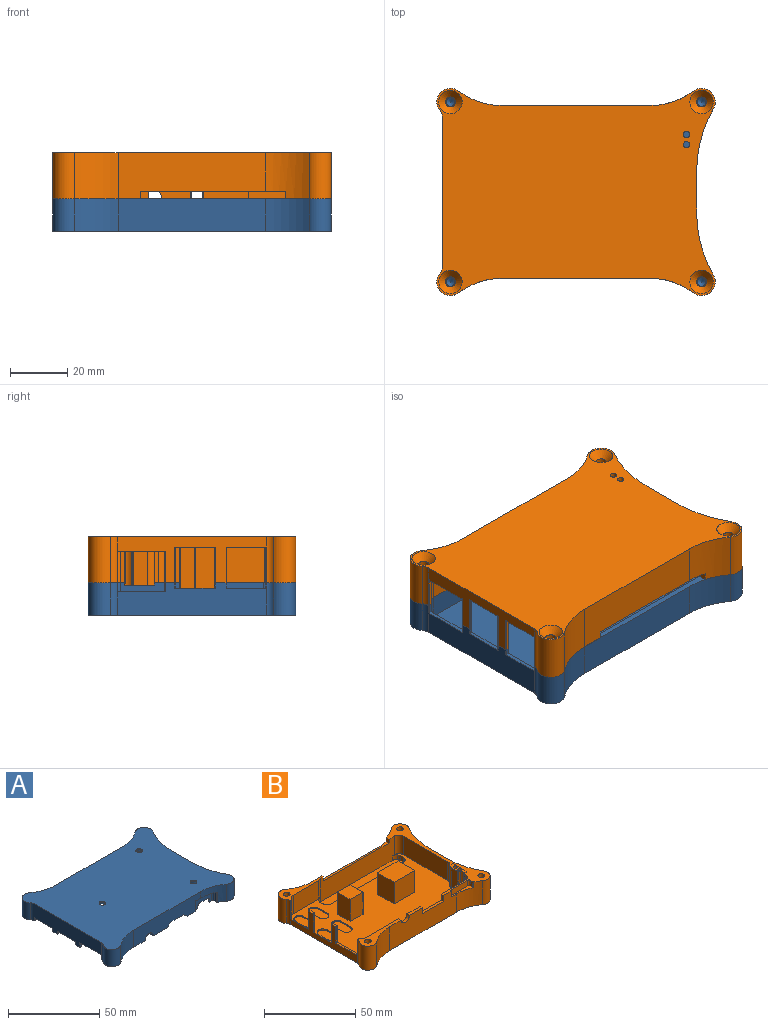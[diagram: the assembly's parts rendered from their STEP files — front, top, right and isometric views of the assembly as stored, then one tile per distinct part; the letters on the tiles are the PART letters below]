
ASSEMBLY  parts=2 mates=1
PART A: 96 faces, bbox 97.3x72.4x11.4 mm
  f0: cylinder r=1.6mm len=1.6mm, axis (0,-1,0), area 2.4mm2, adj f1,f2,f45,f55
  f1: plane 1.58x0.96mm, normal (1,0,0), area 1.5mm2, adj f0,f45,f55,f72
  f2: plane 5.69x0.96mm, normal (0,0,-1), area 5.5mm2, adj f0,f45,f47,f55
  f3: plane 11.74x2.84mm, normal (1,0,0), area 33.4mm2, adj f6,f8,f11,f71
  f4: plane 11.49x2.84mm, normal (0,-1,0), area 32.7mm2, adj f5,f6,f8,f71
  f5: cylinder r=0.25mm len=2.85mm, axis (0,0,1), area 1.1mm2, adj f4,f6,f7,f71
  f6: plane 12.25x12mm, normal (0,0,-1), area 146.9mm2, adj f3,f4,f5,f7,f8,f9,f10,f11
  f7: plane 11.74x2.84mm, normal (-1,0,0), area 33.4mm2, adj f5,f6,f9,f71
  f8: cylinder r=0.25mm len=2.85mm, axis (0,0,1), area 1.1mm2, adj f3,f4,f6,f71
  f9: cylinder r=0.25mm len=2.85mm, axis (0,0,1), area 1.1mm2, adj f6,f7,f10,f71
  f10: plane 11.49x2.84mm, normal (0,1,0), area 32.7mm2, adj f6,f9,f11,f71
  f11: cylinder r=0.25mm len=2.85mm, axis (0,0,1), area 1.1mm2, adj f3,f6,f10,f71
  f12: cylinder r=0.25mm len=2.03mm, axis (0,0,1), area 0.8mm2, adj f19,f57,f94,f95
  f13: cylinder r=0.23mm len=2.03mm, axis (0,0,-1), area 0.6mm2, adj f19,f43,f69,f70
  f14: cylinder r=3.43mm len=11.43mm, axis (0,0,-1), area 27.9mm2, adj f20,f25,f38,f70,f92
  f15: plane 16.88x1.44mm, normal (0,0,-1), area 19.7mm2, adj f16,f17,f18,f37,f44,f57,f66,f67
  f16: cylinder r=0.25mm len=3.23mm, axis (0,0,1), area 1.3mm2, adj f15,f17,f57,f65
  f17: plane 3.23x0.69mm, normal (0,-1,0), area 2.2mm2, adj f15,f16,f18,f65
  f18: cylinder r=0.25mm len=3.23mm, axis (0,0,1), area 1.3mm2, adj f15,f17,f65,f92
  f19: plane 14.2x1.4mm, normal (0,0,-1), area 16.5mm2, adj f12,f13,f20,f43,f57,f69,f92,f93
  f20: cylinder r=0.23mm len=2.03mm, axis (0,0,-1), area 0.7mm2, adj f14,f19,f69,f70
  f21: cylinder r=1.83mm len=3.66mm, axis (0,0,1), area 9mm2, adj f24,f38
  f22: cylinder r=1.83mm len=3.66mm, axis (0,0,1), area 9mm2, adj f23,f38
  f23: cone r=1.83mm half-angle=41deg, axis (0,0,-1), area 63.9mm2, adj f22,f71
  f24: cone r=1.77mm half-angle=41deg, axis (0,0,-1), area 63.9mm2, adj f21,f71
  f25: cylinder r=4.76mm len=11.43mm, axis (0,0,-1), area 159.2mm2, adj f14,f26,f38,f70
  f26: cylinder r=25.4mm len=15.24mm, axis (0,0,-1), area 186.8mm2, adj f25,f27,f38,f70
  f27: plane 51.56x11.43mm, normal (0,1,0), area 589.4mm2, adj f26,f28,f38,f70
  f28: cylinder r=25.4mm len=15.24mm, axis (0,0,-1), area 186.8mm2, adj f27,f29,f38,f70
  f29: cylinder r=4.76mm len=11.43mm, axis (0,0,-1), area 148.8mm2, adj f28,f30,f38,f70
  f30: cylinder r=44.45mm len=22.05mm, axis (0,0,-1), area 263.7mm2, adj f29,f31,f38,f70
  f31: plane 14.04x11.43mm, normal (1,0,0), area 140.5mm2, adj f30,f32,f38,f70,f80,f81,f82,f83
  f32: cylinder r=44.45mm len=22.05mm, axis (0,0,-1), area 263.7mm2, adj f31,f33,f38,f70
  f33: cylinder r=4.76mm len=11.43mm, axis (0,0,-1), area 148.8mm2, adj f32,f34,f38,f70
  f34: cylinder r=25.4mm len=15.24mm, axis (0,0,-1), area 108.6mm2, adj f33,f38,f46,f51,f52,f70
  f35: cylinder r=25.4mm len=15.24mm, axis (0,0,-1), area 186.8mm2, adj f36,f38,f46,f49
  f36: cylinder r=4.76mm len=11.43mm, axis (0,0,-1), area 159.2mm2, adj f35,f37,f38,f49
  f37: cylinder r=3.43mm len=11.43mm, axis (0,0,-1), area 27.5mm2, adj f15,f36,f38,f49,f66,f92
  f38: plane 97.28x72.39mm, normal (0,0,1), area 5689.1mm2, adj f14,f21,f22,f25,f26,f27,f28,f29
  f39: cylinder r=3.43mm len=8.05mm, axis (0,0,1), area 43.4mm2, adj f40,f45,f70,f71
  f40: plane 49.66x8.05mm, normal (-1,0,0), area 379.9mm2, adj f39,f41,f70,f71,f80,f81,f82,f83
  f41: cylinder r=3.43mm len=8.05mm, axis (0,0,1), area 43.4mm2, adj f40,f42,f70,f71
  f42: plane 78.74x8.05mm, normal (0,-1,0), area 634mm2, adj f41,f43,f70,f71
  f43: cylinder r=3.43mm len=8.05mm, axis (0,0,1), area 40.9mm2, adj f13,f19,f42,f57,f70,f71
  f44: cylinder r=3.43mm len=8.05mm, axis (0,0,1), area 39.2mm2, adj f15,f45,f49,f57,f68,f71
  f45: plane 78.74x8.05mm, normal (0,1,0), area 558.8mm2, adj f0,f1,f2,f39,f44,f47,f48,f49
  f46: plane 51.56x11.43mm, normal (0,-1,0), area 513.2mm2, adj f34,f35,f38,f49,f50,f51,f72,f73
  f47: cylinder r=1.6mm len=1.6mm, axis (0,-1,0), area 2.4mm2, adj f2,f45,f48,f55
  f48: plane 1.58x0.96mm, normal (-1,0,0), area 1.5mm2, adj f45,f47,f55,f70
  f49: plane 31.8x10.25mm, normal (0,0,-1), area 122.7mm2, adj f35,f36,f37,f44,f45,f46,f66,f67
  f50: cylinder r=0.25mm len=6.99mm, axis (0,0,1), area 2.5mm2, adj f46,f51,f56,f72
  f51: plane 14.86x3.37mm, normal (0,0,-1), area 21.6mm2, adj f34,f46,f50,f52,f53,f54,f55,f56
  f52: cylinder r=0.25mm len=6.99mm, axis (0,0,1), area 2mm2, adj f34,f51,f53,f70
  f53: plane 6.99x2.25mm, normal (-1,0,0), area 15.7mm2, adj f51,f52,f54,f70
  f54: cylinder r=0.89mm len=6.99mm, axis (0,0,1), area 9.8mm2, adj f51,f53,f55,f70
  f55: plane 12.7x6.99mm, normal (0,-1,0), area 61.6mm2, adj f0,f1,f2,f47,f48,f51,f54,f56
  f56: cylinder r=0.89mm len=6.99mm, axis (0,0,1), area 8.7mm2, adj f50,f51,f55,f72
  f57: plane 49.66x8.05mm, normal (1,0,0), area 294.6mm2, adj f12,f15,f16,f19,f43,f44,f60,f61
  f58: cylinder r=0.25mm len=2.03mm, axis (0,0,1), area 0.8mm2, adj f59,f61,f65,f92
  f59: plane 2.03x0.69mm, normal (0,1,0), area 1.4mm2, adj f58,f60,f61,f65
  f60: cylinder r=0.25mm len=2.03mm, axis (0,0,1), area 0.8mm2, adj f57,f59,f61,f65
  f61: plane 14.22x1.19mm, normal (0,0,-1), area 16.4mm2, adj f57,f58,f59,f60,f62,f63,f64,f92
  f62: cylinder r=0.25mm len=2.03mm, axis (0,0,1), area 0.8mm2, adj f57,f61,f63,f95
  f63: plane 2.03x0.69mm, normal (0,-1,0), area 1.4mm2, adj f61,f62,f64,f95
  f64: cylinder r=0.25mm len=2.03mm, axis (0,0,1), area 0.8mm2, adj f61,f63,f92,f95
  f65: plane 3.7x1.19mm, normal (0,0,-1), area 4.4mm2, adj f16,f17,f18,f57,f58,f59,f60,f92
  f66: cylinder r=0.25mm len=3.23mm, axis (0,0,1), area 1.3mm2, adj f15,f37,f49,f67
  f67: plane 3.23x0.95mm, normal (0,1,0), area 3.1mm2, adj f15,f49,f66,f68
  f68: cylinder r=0.25mm len=3.23mm, axis (0,0,1), area 1mm2, adj f15,f44,f49,f67
  f69: plane 2.03x0.96mm, normal (0,-1,0), area 1.9mm2, adj f13,f19,f20,f70
  f70: plane 97.28x72.39mm, normal (0,0,-1), area 572.3mm2, adj f13,f14,f20,f25,f26,f27,f28,f29
  f71: plane 85.6x56.52mm, normal (0,0,-1), area 4523.3mm2, adj f3,f4,f5,f7,f8,f9,f10,f11
  f72: plane 9.02x1.91mm, normal (0,0,-1), area 14.7mm2, adj f1,f45,f46,f50,f55,f56,f75
  f73: cylinder r=3.17mm len=6.35mm, axis (0,1,0), area 19mm2, adj f45,f46,f49,f74
  f74: plane 10.39x1.91mm, normal (0,0,-1), area 19.8mm2, adj f45,f46,f73,f77
  f75: plane 3.18x2.54mm, normal (-0.62,0,-0.78), area 7.7mm2, adj f45,f46,f72,f76
  f76: plane 9.53x1.91mm, normal (0,0,-1), area 18.1mm2, adj f45,f46,f75,f77
  f77: plane 3.18x2.54mm, normal (0.62,0,-0.78), area 7.7mm2, adj f45,f46,f74,f76
  f78: cylinder r=1.83mm len=3.66mm, axis (0,0,1), area 9mm2, adj f38,f79
  f79: cone r=1.83mm half-angle=41deg, axis (0,0,-1), area 63.9mm2, adj f71,f78
  f80: cylinder r=0.81mm len=2.03mm, axis (1,0,0), area 5.2mm2, adj f31,f40,f81,f83
  f81: plane 11x2.03mm, normal (0,0,-1), area 22.3mm2, adj f31,f40,f80,f82
  f82: cylinder r=0.81mm len=2.03mm, axis (1,0,0), area 5.2mm2, adj f31,f40,f81,f83
  f83: plane 11x2.03mm, normal (0,0,1), area 22.3mm2, adj f31,f40,f80,f82
  f84: cylinder r=1.52mm len=9.88mm, axis (0,0,1), area 94.6mm2, adj f49,f90
  f85: cylinder r=1.52mm len=9.88mm, axis (0,0,1), area 94.6mm2, adj f70,f91
  f86: cylinder r=1.52mm len=9.88mm, axis (0,0,1), area 94.6mm2, adj f70,f88
  f87: cylinder r=1.52mm len=9.88mm, axis (0,0,1), area 94.6mm2, adj f70,f89
  f88: cone r=0.8mm half-angle=59deg, axis (0,0,-1), area 8.5mm2, adj f86
  f89: cone r=0.8mm half-angle=59deg, axis (0,0,-1), area 8.5mm2, adj f87
  f90: cone r=0.8mm half-angle=59deg, axis (0,0,-1), area 8.5mm2, adj f84
  f91: cone r=0.8mm half-angle=59deg, axis (0,0,-1), area 8.5mm2, adj f85
  f92: plane 52.18x11.43mm, normal (-1,0,0), area 484.5mm2, adj f14,f15,f18,f19,f37,f38,f58,f61
  f93: cylinder r=0.25mm len=2.03mm, axis (0,0,-1), area 0.8mm2, adj f19,f92,f94,f95
  f94: plane 2.03x0.69mm, normal (0,1,0), area 1.4mm2, adj f12,f19,f93,f95
  f95: plane 4.28x1.19mm, normal (0,0,-1), area 5.1mm2, adj f12,f57,f62,f63,f64,f92,f93,f94
PART B: 162 faces, bbox 97.3x72.4x18.3 mm
  f0: cylinder r=1.83mm len=13.48mm, axis (0,0,-1), area 154.9mm2, adj f49,f161
  f1: plane 77.06x12.45mm, normal (0,1,0), area 878.7mm2, adj f2,f5,f57,f102,f103,f104,f111,f112
  f2: cylinder r=3.43mm len=12.45mm, axis (0,0,-1), area 52.5mm2, adj f1,f3,f4,f5,f104,f107
  f3: cylinder r=3.43mm len=1.26mm, axis (0,0,1), area 0.4mm2, adj f2,f4,f97
  f4: plane 18.72x12.45mm, normal (1,0,0), area 63.4mm2, adj f2,f3,f5,f92,f93,f96,f97
  f5: plane 86.79x57.08mm, normal (0,0,1), area 3712.6mm2, adj f1,f2,f4,f6,f7,f8,f9,f10
  f6: cylinder r=0.25mm len=14.66mm, axis (0,0,-1), area 5.8mm2, adj f5,f7,f13,f14
  f7: plane 14.66x9.51mm, normal (0,-1,0), area 139.3mm2, adj f5,f6,f8,f14
  f8: cylinder r=0.25mm len=14.66mm, axis (0,0,-1), area 5.8mm2, adj f5,f7,f9,f14
  f9: plane 14.66x9.51mm, normal (1,0,0), area 139.3mm2, adj f5,f8,f10,f14
  f10: cylinder r=0.25mm len=14.66mm, axis (0,0,-1), area 5.8mm2, adj f5,f9,f11,f14
  f11: plane 14.66x9.51mm, normal (0,1,0), area 139.3mm2, adj f5,f10,f12,f14
  f12: cylinder r=0.25mm len=14.66mm, axis (0,0,-1), area 5.8mm2, adj f5,f11,f13,f14
  f13: plane 14.66x9.51mm, normal (-1,0,0), area 139.3mm2, adj f5,f6,f12,f14
  f14: plane 10.02x10.02mm, normal (0,0,1), area 100.3mm2, adj f6,f7,f8,f9,f10,f11,f12,f13
  f15: plane 14.4x12.51mm, normal (-1,0,0), area 180.1mm2, adj f5,f16,f22,f24,f25,f27
  f16: cylinder r=0.25mm len=14.15mm, axis (0,0,-1), area 5.6mm2, adj f5,f15,f17,f27
  f17: plane 15.58x14.4mm, normal (0,1,0), area 224.3mm2, adj f5,f16,f18,f22,f26,f27
  f18: cylinder r=0.25mm len=14.15mm, axis (0,0,-1), area 5.6mm2, adj f5,f17,f19,f26
  f19: plane 14.4x12.51mm, normal (1,0,0), area 180.1mm2, adj f5,f18,f20,f21,f22,f26
  f20: cylinder r=0.25mm len=14.15mm, axis (0,0,-1), area 5.6mm2, adj f5,f19,f21,f23
  f21: cylinder r=0.25mm len=0.25mm, axis (0,0,-1), area 0.1mm2, adj f19,f20,f22,f23
  f22: plane 16.08x13.02mm, normal (0,0,1), area 209.3mm2, adj f15,f17,f19,f21,f23,f25,f26,f27
  f23: plane 15.58x14.4mm, normal (0,-1,0), area 224.3mm2, adj f5,f20,f21,f22,f24,f25
  f24: cylinder r=0.25mm len=14.15mm, axis (0,0,-1), area 5.6mm2, adj f5,f15,f23,f25
  f25: cylinder r=0.25mm len=0.25mm, axis (0,0,-1), area 0.1mm2, adj f15,f22,f23,f24
  f26: cylinder r=0.25mm len=0.25mm, axis (0,0,-1), area 0.1mm2, adj f17,f18,f19,f22
  f27: cylinder r=0.25mm len=0.25mm, axis (0,0,-1), area 0.1mm2, adj f15,f16,f17,f22
  f28: plane 6.86x0.76mm, normal (-1,0,0), area 5.2mm2, adj f5,f29,f30,f31
  f29: cylinder r=3.17mm len=6.35mm, axis (0,0,-1), area 7.6mm2, adj f5,f28,f30,f32
  f30: plane 13.21x6.35mm, normal (0,0,1), area 75.2mm2, adj f28,f29,f31,f32
  f31: cylinder r=3.17mm len=6.35mm, axis (0,0,-1), area 7.6mm2, adj f5,f28,f30,f32
  f32: plane 6.86x0.76mm, normal (1,0,0), area 5.2mm2, adj f5,f29,f30,f31
  f33: plane 6.86x0.76mm, normal (1,0,0), area 5.2mm2, adj f5,f34,f36,f37
  f34: cylinder r=3.17mm len=6.35mm, axis (0,0,-1), area 7.6mm2, adj f5,f33,f35,f37
  f35: plane 6.86x0.76mm, normal (-1,0,0), area 5.2mm2, adj f5,f34,f36,f37
  f36: cylinder r=3.17mm len=6.35mm, axis (0,0,-1), area 7.6mm2, adj f5,f33,f35,f37
  f37: plane 13.21x6.35mm, normal (0,0,1), area 75.2mm2, adj f33,f34,f35,f36
  f38: plane 6.99x0.76mm, normal (1,0,0), area 5.3mm2, adj f5,f39,f40,f41
  f39: cylinder r=3.17mm len=6.35mm, axis (0,0,-1), area 7.6mm2, adj f5,f38,f40,f42
  f40: plane 13.34x6.35mm, normal (0,0,1), area 76mm2, adj f38,f39,f41,f42
  f41: cylinder r=3.17mm len=6.35mm, axis (0,0,-1), area 7.6mm2, adj f5,f38,f40,f42
  f42: plane 6.99x0.76mm, normal (-1,0,0), area 5.3mm2, adj f5,f39,f40,f41
  f43: plane 6.99x0.76mm, normal (1,0,0), area 5.3mm2, adj f5,f44,f45,f46
  f44: cylinder r=3.17mm len=6.35mm, axis (0,0,-1), area 7.6mm2, adj f5,f43,f45,f47
  f45: plane 13.34x6.35mm, normal (0,0,1), area 76mm2, adj f43,f44,f46,f47
  f46: cylinder r=3.17mm len=6.35mm, axis (0,0,-1), area 7.6mm2, adj f5,f43,f45,f47
  f47: plane 6.99x0.76mm, normal (-1,0,0), area 5.3mm2, adj f5,f44,f45,f46
  f48: plane 97.28x72.39mm, normal (0,0,-1), area 5503.1mm2, adj f50,f51,f52,f54,f56,f87,f88,f89
  f49: plane 30.57x10.34mm, normal (0,0,1), area 115.3mm2, adj f0,f50,f51,f63,f66,f67,f82,f83
  f50: cylinder r=25.4mm len=16.08mm, axis (0,0,1), area 262.8mm2, adj f48,f49,f51,f88
  f51: plane 51.56x16.08mm, normal (0,1,0), area 717.7mm2, adj f48,f49,f50,f52,f64,f66
  f52: cylinder r=25.4mm len=16.08mm, axis (0,0,1), area 244.9mm2, adj f48,f51,f57,f64,f65,f133
  f53: cylinder r=1.83mm len=13.48mm, axis (0,0,-1), area 154.9mm2, adj f54,f57
  f54: cone r=1.83mm half-angle=41deg, axis (0,0,-1), area 63.9mm2, adj f48,f53
  f55: cylinder r=1.83mm len=13.48mm, axis (0,0,-1), area 154.9mm2, adj f56,f57
  f56: cone r=1.83mm half-angle=41deg, axis (0,0,-1), area 63.9mm2, adj f48,f55
  f57: plane 72.39x32.87mm, normal (0,0,1), area 376.6mm2, adj f1,f52,f53,f55,f58,f59,f60,f61
  f58: plane 1.18x0.94mm, normal (0,-1,0), area 1.1mm2, adj f57,f158,f159,f160
  f59: plane 2.12x0.94mm, normal (0,1,0), area 2mm2, adj f57,f151,f152,f160
  f60: cylinder r=3.43mm len=12.45mm, axis (0,0,-1), area 33.8mm2, adj f5,f57,f61,f142
  f61: plane 34.64x12.45mm, normal (-1,0,0), area 431.2mm2, adj f5,f57,f60,f62
  f62: cylinder r=3.43mm len=12.45mm, axis (0,0,1), area 67mm2, adj f5,f57,f61,f63
  f63: plane 57.06x15.52mm, normal (0,-1,0), area 751.3mm2, adj f5,f49,f57,f62,f64,f65,f66,f67
  f64: plane 50.8x2.31mm, normal (0,0,1), area 70.5mm2, adj f51,f52,f63,f65,f66
  f65: plane 2.54x2.31mm, normal (-1,0,0), area 5.9mm2, adj f52,f57,f63,f64
  f66: plane 2.54x1.34mm, normal (1,0,0), area 3.4mm2, adj f49,f51,f63,f64
  f67: cylinder r=3.43mm len=12.45mm, axis (0,0,-1), area 24.7mm2, adj f49,f63,f81,f82
  f68: cylinder r=3.43mm len=3.07mm, axis (0,0,-1), area 10.4mm2, adj f5,f69,f80,f81
  f69: plane 3.07x1.78mm, normal (1,0,0), area 5.5mm2, adj f5,f68,f70,f80
  f70: cylinder r=3.43mm len=3.43mm, axis (0,0,-1), area 16.6mm2, adj f5,f69,f71,f80
  f71: plane 55.37x3.07mm, normal (0,1,0), area 170.2mm2, adj f5,f70,f72,f80
  f72: cylinder r=3.43mm len=3.07mm, axis (0,0,-1), area 5.2mm2, adj f5,f71,f73,f80
  f73: cylinder r=3.43mm len=3.07mm, axis (0,0,-1), area 0.4mm2, adj f5,f72,f74,f80
  f74: cylinder r=3.43mm len=3.07mm, axis (0,0,-1), area 3.1mm2, adj f5,f73,f75,f80
  f75: cylinder r=3.43mm len=3.07mm, axis (0,0,-1), area 7.1mm2, adj f5,f74,f76,f80
  f76: cylinder r=3.43mm len=3.07mm, axis (0,0,-1), area 0.7mm2, adj f5,f75,f77,f80
  f77: plane 3.07x1.78mm, normal (-1,0,0), area 5.5mm2, adj f5,f76,f78,f80
  f78: cylinder r=3.43mm len=3.07mm, axis (0,0,-1), area 5.7mm2, adj f5,f77,f79,f80
  f79: cylinder r=3.43mm len=3.07mm, axis (0,0,-1), area 10.8mm2, adj f5,f63,f78,f80
  f80: plane 62.23x8.64mm, normal (0,0,1), area 527.3mm2, adj f63,f68,f69,f70,f71,f72,f73,f74
  f81: cylinder r=3.43mm len=3.07mm, axis (0,0,-1), area 6.1mm2, adj f63,f67,f68,f80
  f82: plane 19.81x12.45mm, normal (0,-1,0), area 246.5mm2, adj f5,f49,f67,f83
  f83: cylinder r=3.43mm len=12.45mm, axis (0,0,-1), area 52.1mm2, adj f5,f49,f82,f84
  f84: cylinder r=0.23mm len=12.45mm, axis (0,0,1), area 3.5mm2, adj f5,f49,f83,f85
  f85: plane 12.45x0.96mm, normal (0,-1,0), area 11.9mm2, adj f5,f49,f84,f86
  f86: cylinder r=0.23mm len=12.45mm, axis (0,0,1), area 4.5mm2, adj f5,f49,f85,f87
  f87: cylinder r=3.43mm len=16.08mm, axis (0,0,1), area 39.2mm2, adj f48,f49,f86,f88,f89
  f88: cylinder r=4.76mm len=16.08mm, axis (0,0,1), area 224mm2, adj f48,f49,f50,f87
  f89: plane 52.18x16.08mm, normal (-1,0,0), area 301.9mm2, adj f5,f48,f87,f90,f93,f94,f97,f98
  f90: cylinder r=0.25mm len=12.45mm, axis (0,0,-1), area 5mm2, adj f5,f89,f91,f93
  f91: plane 12.45x0.69mm, normal (0,1,0), area 8.5mm2, adj f5,f90,f92,f93
  f92: cylinder r=0.25mm len=12.45mm, axis (0,0,-1), area 5mm2, adj f4,f5,f91,f93
  f93: plane 3.7x1.19mm, normal (0,0,1), area 4.4mm2, adj f4,f89,f90,f91,f92,f94,f95,f96
  f94: cylinder r=0.25mm len=10.92mm, axis (0,0,-1), area 4.4mm2, adj f89,f93,f95,f97
  f95: plane 10.92x0.69mm, normal (0,-1,0), area 7.5mm2, adj f93,f94,f96,f97
  f96: cylinder r=0.25mm len=10.92mm, axis (0,0,-1), area 4.4mm2, adj f4,f93,f95,f97
  f97: plane 16.79x1.43mm, normal (0,0,1), area 19.7mm2, adj f3,f4,f89,f94,f95,f96,f107,f108
  f98: cylinder r=3.43mm len=16.08mm, axis (0,0,1), area 39.1mm2, adj f48,f89,f99,f104,f109
  f99: cylinder r=4.76mm len=16.08mm, axis (0,0,1), area 224mm2, adj f48,f98,f100,f104
  f100: cylinder r=25.4mm len=16.08mm, axis (0,0,1), area 262.8mm2, adj f48,f99,f101,f104
  f101: plane 51.56x16.08mm, normal (0,-1,0), area 733.4mm2, adj f48,f57,f100,f102,f103,f104,f113,f115
  f102: plane 10.39x1.91mm, normal (0,0,1), area 19.8mm2, adj f1,f101,f103,f110,f111,f120
  f103: cylinder r=3.17mm len=6.35mm, axis (0,-1,0), area 19mm2, adj f1,f101,f102,f104
  f104: plane 31.8x10.25mm, normal (0,0,1), area 119.5mm2, adj f1,f2,f98,f99,f100,f101,f103,f105
  f105: cylinder r=1.83mm len=13.48mm, axis (0,0,-1), area 154.9mm2, adj f104,f106
  f106: cone r=1.83mm half-angle=41deg, axis (0,0,-1), area 63.9mm2, adj f48,f105
  f107: cylinder r=0.23mm len=10.92mm, axis (0,0,1), area 3mm2, adj f2,f97,f104,f108
  f108: plane 10.92x1.07mm, normal (0,1,0), area 11.7mm2, adj f97,f104,f107,f109
  f109: cylinder r=0.15mm len=10.92mm, axis (0,0,-1), area 2.6mm2, adj f97,f98,f104,f108
  f110: plane 3.94x1.4mm, normal (1,0,0), area 5.5mm2, adj f102,f111,f112,f113,f119,f120
  f111: cylinder r=0.25mm len=3.56mm, axis (0,0,1), area 1.4mm2, adj f1,f102,f110,f112
  f112: cylinder r=0.25mm len=0.38mm, axis (0,0,1), area 0.2mm2, adj f1,f110,f111,f113
  f113: plane 16.38x1.91mm, normal (0,0,1), area 30.3mm2, adj f1,f101,f110,f112,f114,f116,f118,f119
  f114: plane 3.94x1.4mm, normal (-1,0,0), area 5.5mm2, adj f57,f113,f115,f116,f117,f118
  f115: cylinder r=0.25mm len=3.56mm, axis (0,0,-1), area 1.4mm2, adj f57,f101,f114,f116
  f116: cylinder r=0.25mm len=0.38mm, axis (0,0,1), area 0.2mm2, adj f101,f113,f114,f115
  f117: cylinder r=0.25mm len=3.56mm, axis (0,0,-1), area 1.4mm2, adj f1,f57,f114,f118
  f118: cylinder r=0.25mm len=0.38mm, axis (0,0,1), area 0.2mm2, adj f1,f113,f114,f117
  f119: cylinder r=0.25mm len=0.38mm, axis (0,0,1), area 0.2mm2, adj f101,f110,f113,f120
  f120: cylinder r=0.25mm len=3.56mm, axis (0,0,1), area 1.4mm2, adj f101,f102,f110,f119
  f121: cylinder r=25.4mm len=16.08mm, axis (0,0,1), area 220.1mm2, adj f48,f57,f101,f122,f123,f129
  f122: plane 14.86x3.37mm, normal (0,0,1), area 21.6mm2, adj f101,f121,f123,f124,f125,f126,f127,f128
  f123: cylinder r=0.25mm len=3.81mm, axis (0,0,-1), area 1.1mm2, adj f57,f121,f122,f124
  f124: plane 3.81x2.25mm, normal (-1,0,0), area 8.6mm2, adj f57,f122,f123,f125
  f125: cylinder r=0.89mm len=3.81mm, axis (0,0,-1), area 5.3mm2, adj f57,f122,f124,f126
  f126: plane 12.7x3.81mm, normal (0,-1,0), area 48.4mm2, adj f57,f122,f125,f127
  f127: cylinder r=0.89mm len=3.81mm, axis (0,0,-1), area 4.7mm2, adj f57,f122,f126,f128
  f128: cylinder r=0.25mm len=3.81mm, axis (0,0,-1), area 1.3mm2, adj f57,f101,f122,f127
  f129: cylinder r=4.76mm len=16.08mm, axis (0,0,1), area 209.3mm2, adj f48,f57,f121,f130
  f130: cylinder r=44.45mm len=22.05mm, axis (0,0,1), area 371mm2, adj f48,f57,f129,f131
  f131: plane 16.08x14.04mm, normal (1,0,0), area 225.7mm2, adj f48,f57,f130,f132
  f132: cylinder r=44.45mm len=22.05mm, axis (0,0,1), area 371mm2, adj f48,f57,f131,f133
  f133: cylinder r=4.76mm len=16.08mm, axis (0,0,1), area 209.3mm2, adj f48,f52,f57,f132
  f134: cylinder r=0.25mm len=12.45mm, axis (0,0,-1), area 5mm2, adj f5,f89,f135,f138
  f135: plane 12.45x0.69mm, normal (0,-1,0), area 8.5mm2, adj f5,f134,f136,f138
  f136: cylinder r=0.25mm len=12.45mm, axis (0,0,-1), area 5mm2, adj f5,f135,f137,f138
  f137: plane 12.45x3.78mm, normal (1,0,0), area 47mm2, adj f5,f136,f138,f141
  f138: plane 4.28x1.19mm, normal (0,0,1), area 5.1mm2, adj f89,f134,f135,f136,f137,f139,f140,f141
  f139: cylinder r=0.25mm len=12.45mm, axis (0,0,1), area 5mm2, adj f5,f89,f138,f140
  f140: plane 12.45x0.69mm, normal (0,1,0), area 8.5mm2, adj f5,f138,f139,f141
  f141: cylinder r=0.25mm len=12.45mm, axis (0,0,-1), area 5mm2, adj f5,f137,f138,f140
  f142: plane 12.45x1.44mm, normal (-0.7,0.71,0), area 25.2mm2, adj f5,f57,f60,f143
  f143: cylinder r=3.43mm len=12.45mm, axis (0,0,-1), area 1.7mm2, adj f5,f57,f142,f150
  f144: plane 9.97x0.94mm, normal (1,0,0), area 9.4mm2, adj f57,f152,f159,f160
  f145: plane 13.39x4.89mm, normal (-1,0,0), area 65.4mm2, adj f5,f150,f155,f160
  f146: cylinder r=3.43mm len=12.45mm, axis (0,0,-1), area 2.9mm2, adj f5,f57,f147,f157
  f147: plane 12.45x1.22mm, normal (-1,0,0), area 15.2mm2, adj f5,f57,f146,f148
  f148: cylinder r=3.43mm len=12.45mm, axis (0,0,-1), area 23.1mm2, adj f5,f57,f147,f149
  f149: cylinder r=3.43mm len=12.45mm, axis (0,0,-1), area 43.9mm2, adj f1,f5,f57,f148
  f150: cylinder r=3.43mm len=13.39mm, axis (0,0,-1), area 34.6mm2, adj f5,f143,f145,f151,f160
  f151: cylinder r=0.25mm len=0.94mm, axis (0,0,-1), area 0.2mm2, adj f57,f59,f150,f160
  f152: cylinder r=0.25mm len=0.94mm, axis (0,0,-1), area 0.4mm2, adj f57,f59,f144,f160
  f153: cylinder r=1.1mm len=17.02mm, axis (0,0,1), area 118.1mm2, adj f48,f160
  f154: cylinder r=1.1mm len=17.02mm, axis (0,0,1), area 118.1mm2, adj f48,f160
  f155: cylinder r=0.25mm len=13.39mm, axis (0,0,-1), area 3.5mm2, adj f5,f145,f156,f160
  f156: cylinder r=3.43mm len=13.39mm, axis (0,0,-1), area 13.5mm2, adj f5,f155,f157,f160
  f157: cylinder r=3.43mm len=13.39mm, axis (0,0,-1), area 30.8mm2, adj f5,f146,f156,f158,f160
  f158: cylinder r=0.25mm len=0.94mm, axis (0,0,-1), area 0.4mm2, adj f57,f58,f157,f160
  f159: cylinder r=0.25mm len=0.94mm, axis (0,0,-1), area 0.4mm2, adj f57,f58,f144,f160
  f160: plane 10.48x3.48mm, normal (0,0,1), area 24.2mm2, adj f58,f59,f144,f145,f150,f151,f152,f153
  f161: cone r=1.83mm half-angle=41deg, axis (0,0,-1), area 64.1mm2, adj f0,f48
PLACE A rot(axis=(1,0,0),180deg) t=(-49.11,-95.64,5.72)mm
PLACE B rot(axis=(1,0,0),180deg) t=(0,-62.87,27.89)mm
MATE fastened A.f85 <-> B.f0  axis (0,0,1) through (0,-62.87,11.43)mm
